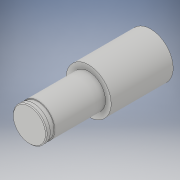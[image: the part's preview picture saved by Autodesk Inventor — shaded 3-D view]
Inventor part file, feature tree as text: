
AUTODESK INVENTOR PART (.ipt)
format: ipt  version: 2018 (Build 220112000, 112)  size: 118,272 bytes
history: native  units: mm
features: revolve x1, sketch x1
ambient origin geometry x8: Origin, YZ Plane, XZ Plane, XY Plane, X Axis, Y Axis, Z Axis, Center Point
bodies: Solid1 (feature_tree)
feature tree (2):
  revolve  "Revolution1"  [1 undecoded]
  sketch  "Sketch1"  dims[d0=21.5mm d1=0.15mm d2=0.15mm d3=0.7mm d4=0.15mm d5=0.8mm d6=11.0mm d7=9.0mm d8=4.0mm d9=3.0mm d10=90.0deg]
note: 1 required parameter value undecoded (feature->parameter linkage not recoverable at this tier; creation-order binding heuristic only, values carry confidence <= 0.55)
